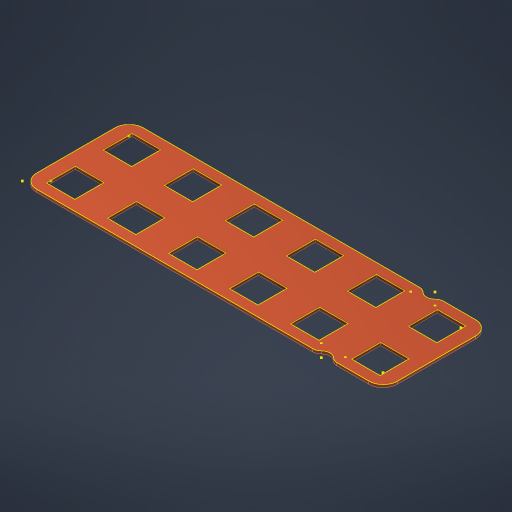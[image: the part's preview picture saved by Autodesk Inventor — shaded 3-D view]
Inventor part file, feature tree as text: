
AUTODESK INVENTOR PART (.ipt)
format: ipt  version: 2024.3 (Build 283343010, 343A)  size: 343,040 bytes
history: native  units: mm
features: fillet x2, sketch x2, extrude x1, projected_geometry x1
ambient origin geometry x8: Origin, YZ Plane, XZ Plane, XY Plane, X Axis, Y Axis, Z Axis, Center Point
bodies: Volumenkörper1 (feature_tree)
feature tree (6):
  extrude  "Extrusion1"  Depth=37.5mm
  fillet  "Rundung1"  Radius=10.2mm
  fillet  "Rundung2"  Radius=10.0mm
  sketch  "Skizze2"  dims[d4=20.0mm d6=20.0mm d7=60.0mm d9=21.5mm d13=5.75mm d14=1.0mm d15=0.0mm d16=5.0mm d17=43.0mm d18=21.5mm d19=10.0mm d20=3.0mm d21=1.25mm d22=10.75mm d23=1.25mm d24=3.0mm]
  sketch  "Skizze1"  dims[d0=127.0mm d1=37.5mm d2=10.2mm d3=10.0mm]
  projected_geometry  "Projizierte Kontur1"
